# Revit family: ЗК РАШВОРК арт.101
name_source: partatom
category: Арматура трубопроводов
units: mm (PartAtom-declared; Revit-internal decimal feet)

## family parameters
Всегда вертикально = Да
На основе рабочей плоскости = Нет
Общий = Нет
При загрузке вырезать с полостями = Нет
Размер круглого соединителя = Использовать диаметр
Тип детали = Нормальный

## types (15) — shared parameters
ADSK_Завод-изготовитель = ООО ТД "РАШВОРК"
H2 = 60 мм
HH = 28 мм
L2 = 16 мм
URL = https://rwru.ru
Корпус = GGG40
zero-valued in all types: Отметка по умолчанию

## per-type parameters (varying)
| type | ADSK_Единица измерения | ADSK_Масса | ADSK_Наименование краткое | B | D | D1 | DN | DNсоединителя | G | H | H1 | L | L1 | V1 | f | Высота | Длина | Штурвал |
| Задвижка с обрезиненным клином РАШВОРК 101-040-16, DN40, PN16, корпус - GJS-500-7 (GGG50), клин - GJS-500-7 (GGG50), уплотнение - EPDM, Ф/Ф, штурвал | ШТ | 9.5 | 101-040-16 | 19 мм | 150 мм | 30 мм | 40 мм | 40 мм | 84 мм | 230 мм | 148 мм | 140 мм | 60 мм | 112 мм | 3 мм | 70 мм | 342 мм | Штурвал : 160 |
| Задвижка с обрезиненным клином РАШВОРК 101-050-16, DN50, PN16, корпус - GJS-500-7 (GGG50), клин - GJS-500-7 (GGG50), уплотнение - EPDM, Ф/Ф, штурвал | шт | 10 | 101-050-16 | 19 мм | 165 мм | 35 мм | 50 мм | 50 мм | 99 мм | 236 мм | 166 мм | 150 мм | 42 мм | 126 мм | 3 мм | 75 мм | 400 мм | Штурвал : 180 |
| Задвижка с обрезиненным клином РАШВОРК 101-065-16, DN65, PN16, корпус - GJS-500-7 (GGG50), клин - GJS-500-7 (GGG50), уплотнение - EPDM, Ф/Ф, штурвал | шт | 12.5 | 101-065-16 | 19 мм | 185 мм | 45 мм | 65 мм | 65 мм | 118 мм | 258 мм | 200 мм | 170 мм | 105 мм | 112 мм | 3 мм | 85 мм | 342 мм | Штурвал : 180 |
| Задвижка с обрезиненным клином РАШВОРК 101-080-16, DN80, PN16, корпус - GJS-500-7 (GGG50), клин - GJS-500-7 (GGG50), уплотнение - EPDM, Ф/Ф, штурвал | шт | 15.5 | 101-080-16 | 19 мм | 200 мм | 52 мм | 80 мм | 80 мм | 132 мм | 289 мм | 218 мм | 180 мм | 125 мм | 160 мм | 3 мм | 90 мм | 342 мм | Штурвал : 200 |
| Задвижка с обрезиненным клином РАШВОРК 101-100-16, DN100, PN16, корпус - GJS-500-7 (GGG50), клин - GJS-500-7 (GGG50), уплотнение - EPDM, Ф/Ф, штурвал | шт | 18.5 | 101-100-16 | 19 мм | 220 мм | 60 мм | 100 мм | 100 мм | 156 мм | 319 мм | 254 мм | 190 мм | 120 мм | 180 мм | 3 мм | 95 мм | 342 мм | Штурвал : 250 |
| Задвижка с обрезиненным клином РАШВОРК 101-125-16, DN125, PN16, корпус - GJS-500-7 (GGG50), клин - GJS-500-7 (GGG50), уплотнение - EPDM, Ф/Ф, штурвал | шт | 26.5 | 101-125-16 | 19 мм | 250 мм | 80 мм | 125 мм | 125 мм | 184 мм | 361 мм | 289 мм | 200 мм | 130 мм | 230 мм | 3 мм | 100 мм | 342 мм | Штурвал : 280 |
| Задвижка с обрезиненным клином РАШВОРК 101-150-16, DN150, PN16, корпус - GJS-500-7 (GGG50), клин - GJS-500-7 (GGG50), уплотнение - EPDM, Ф/Ф, штурвал | шт | 32 | 101-150-16 | 19 мм | 285 мм | 90 мм | 150 мм | 150 мм | 211 мм | 398 мм | 330 мм | 210 мм | 130 мм | 260 мм | 3 мм | 105 мм | 342 мм | Штурвал : 280 |
| Задвижка с обрезиненным клином РАШВОРК 101-200-16, DN200, PN16, корпус - GJS-500-7 (GGG50), клин - GJS-500-7 (GGG50), уплотнение - EPDM, Ф/Ф, штурвал | шт | 52 | 101-200-16 | 20 мм | 340 мм | 110 мм | 200 мм | 200 мм | 266 мм | 492 мм | 409 мм | 230 мм | 150 мм | 310 мм | 3 мм | 115 мм | 342 мм | Штурвал : 340 |
| Задвижка с обрезиненным клином РАШВОРК 101-250-16, DN250, PN16, корпус - GJS-500-7 (GGG50), клин - GJS-500-7 (GGG50), уплотнение - EPDM, Ф/Ф, штурвал | шт | 80 | 101-250-16 | 22 мм | 405 мм | 125 мм | 250 мм | 250 мм | 319 мм | 571 мм | 476 мм | 250 мм | 170 мм | 370 мм | 3 мм | 125 мм | 342 мм | Штурвал : 340 |
| Задвижка с обрезиненным клином РАШВОРК 101-300-16, DN300, PN16, корпус - GJS-500-7 (GGG50), клин - GJS-500-7 (GGG50), уплотнение - EPDM, Ф/Ф, штурвал | шт | 110 | 101-300-16 | 25 мм | 460 мм | 164 мм | 300 мм | 300 мм | 370 мм | 663 мм | 544 мм | 270 мм | 170 мм | 410 мм | 4 мм | 135 мм | 342 мм | Штурвал : 400 |
| Задвижка с обрезиненным клином РАШВОРК 101-350-16, DN350, PN16, корпус - GJS-500-7 (GGG50), клин - GJS-500-7 (GGG50), уплотнение - EPDM, Ф/Ф, штурвал | шт | 210 | 101-350-16 | 27 мм | 520 мм | 198 мм | 350 мм | 350 мм | 429 мм | 800 мм | 724 мм | 290 мм | 210 мм | 530 мм | 4 мм | 145 мм | 342 мм | Штурвал : 450 |
| Задвижка с обрезиненным клином РАШВОРК 101-400-16, DN400, PN16, корпус - GJS-500-7 (GGG50), клин - GJS-500-7 (GGG50), уплотнение - EPDM, Ф/Ф, штурвал | шт | 269 | 101-400-16 | 28 мм | 580 мм | 220 мм | 400 мм | 400 мм | 480 мм | 880 мм | 762 мм | 310 мм | 210 мм | 595 мм | 4 мм | 155 мм | 342 мм | Штурвал : 450 |
| Задвижка с обрезиненным клином РАШВОРК 101-450-16, DN450, PN16, корпус - GJS-500-7 (GGG50), клин - GJS-500-7 (GGG50), уплотнение - EPDM, Ф/Ф, штурвал | шт | 338 | 101-450-16 | 30 мм | 640 мм | 235 мм | 450 мм | 450 мм | 548 мм | 958 мм | 810 мм | 330 мм | 220 мм | 630 мм | 4 мм | 165 мм | 342 мм | Штурвал : 450 |
| Задвижка с обрезиненным клином РАШВОРК 101-500-16, DN500, PN16, корпус - GJS-500-7 (GGG50), клин - GJS-500-7 (GGG50), уплотнение - EPDM, Ф/Ф, штурвал | шт | 442 | 101-500-16 | 32 мм | 715 мм | 275 мм | 500 мм | 500 мм | 609 мм | 1004 мм | 932 мм | 350 мм | 284 мм | 700 мм | 4 мм | 175 мм | 342 мм | Штурвал : 600 |
| Задвижка с обрезиненным клином РАШВОРК 101-600-16, DN600, PN16, корпус - GJS-500-7 (GGG50), клин - GJS-500-7 (GGG50), уплотнение - EPDM, Ф/Ф, штурвал | шт | 660 | 101-600-16 | 36 мм | 840 мм | 300 мм | 600 мм | 600 мм | 720 мм | 1157 мм | 1052 мм | 390 мм | 312 мм | 775 мм | 5 мм | 195 мм | 342 мм | Штурвал : 600 |

note: column(s) folded — value = type name in every type: ADSK_Наименование

## geometry (parser evidence)
native form markers: Blend x4
no freeform markers — native parametric forms only
